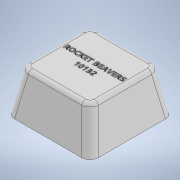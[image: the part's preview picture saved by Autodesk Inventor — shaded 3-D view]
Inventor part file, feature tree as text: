
AUTODESK INVENTOR PART (.ipt)
format: ipt  version: 2020 (Build 240168000, 168)  size: 523,776 bytes
history: native  units: in
note: dims shown in document units (in); Inventor stores cm internally (conversion verified against a paired STEP export)
features: chamfer x4, sketch x3, extrude x2, fillet x2, emboss x1
ambient origin geometry x8: Origin, YZ Plane, XZ Plane, XY Plane, X Axis, Y Axis, Z Axis, Center Point
bodies: Solid1 (feature_tree)
feature tree (12):
  extrude  "Extrusion1"  Depth=1.0in
  chamfer  "Chamfer1"  Distance=1.0in
  chamfer  "Chamfer2"  Distance=1.0in Angle=45.0deg
  chamfer  "Chamfer3"  Distance=1.0in Angle=45.0deg
  chamfer  "Chamfer4"  Distance=1.0in Angle=45.0deg
  fillet  "Fillet1"  Radius=0.1in
  fillet  "Fillet2"  Radius=0.2in
  emboss  "Emboss1"
  extrude  "Extrusion2"  Depth=1.0in
  sketch  "Sketch1"  dims[d0=2.0in d1=2.0in d2=1.0in d3=0.0in d4=0.18in d5=1.0in d6=45.0deg d7=0.18in d8=1.0in d9=45.0deg d10=0.18in d11=1.0in d12=45.0deg]
  sketch  "Sketch3"  dims[d13=0.18in d14=1.0in d15=45.0deg d16=0.1in d17=0.2in]
  sketch  "Sketch4"  dims[d19=1.0in d20=1.0in d21=0.1in d22=0.0in d23=1.0in d24=1.0in d25=0.24in d26=0.5in d27=0.48in d28=1.0in d29=0.22in d30=0.0in]
